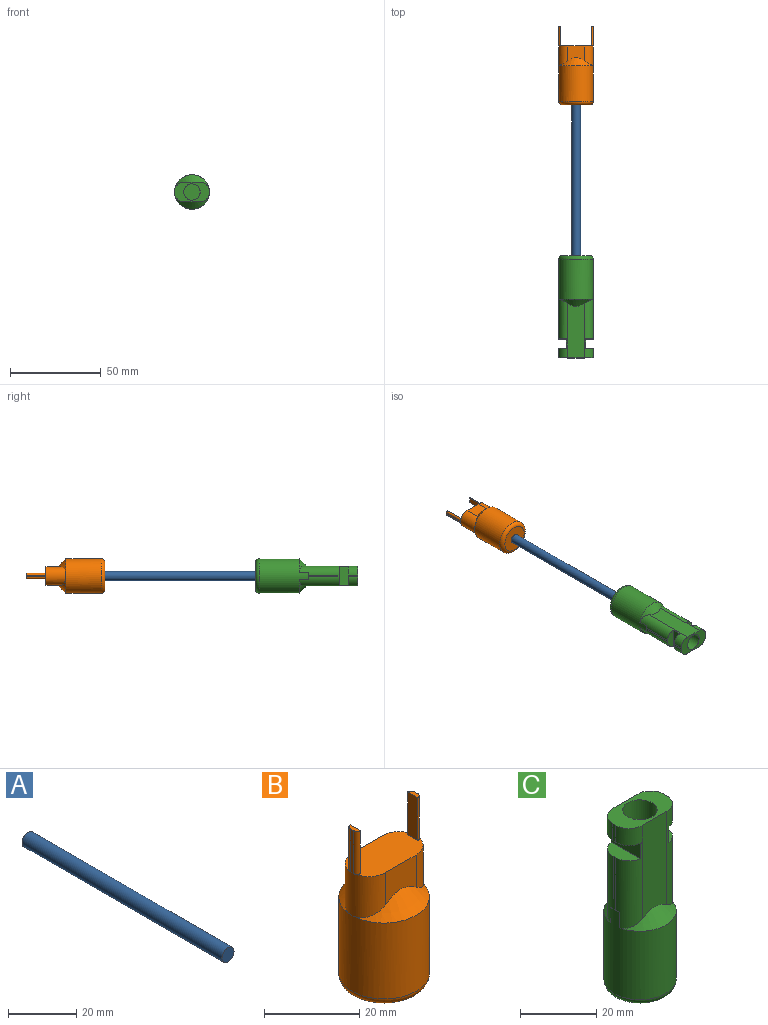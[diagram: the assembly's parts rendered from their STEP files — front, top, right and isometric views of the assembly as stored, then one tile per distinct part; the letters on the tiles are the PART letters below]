
ASSEMBLY  parts=3 mates=2
PART A: 3 faces, bbox 5x83x5 mm
  f0: cylinder r=2.5mm len=83mm, axis (0,1,0), area 1303.8mm2, adj f1,f2
  f1: plane 5x5mm, normal (0,-1,0), area 19.6mm2, adj f0
  f2: plane 5x5mm, normal (0,1,0), area 19.6mm2, adj f0
PART B: 24 faces, bbox 20.6x20.6x43.5 mm
  f0: plane 18.84x10mm, normal (0,0,1), area 163.5mm2, adj f5,f6,f7,f8,f13,f17,f19,f20
  f1: cone r=4.5mm half-angle=45deg, axis (0,0,-1), area 81.3mm2, adj f3,f6,f7,f8
  f2: plane 15x15mm, normal (0,0,-1), area 176.7mm2, adj f23
  f3: cylinder r=9.5mm len=19.5mm, axis (0,0,1), area 1164mm2, adj f1,f4,f23
  f4: cone r=4.5mm half-angle=45deg, axis (0,0,-1), area 81.3mm2, adj f3,f5,f7,f8
  f5: plane 9.01x8.23mm, normal (0,-1,0), area 64mm2, adj f0,f4,f7,f8
  f6: plane 9.01x8.23mm, normal (0,1,0), area 64mm2, adj f0,f1,f7,f8
  f7: cylinder r=5mm len=11mm, axis (0,0,1), area 158mm2, adj f0,f1,f4,f5,f6,f14,f15
  f8: cylinder r=5mm len=11mm, axis (0,0,-1), area 158mm2, adj f0,f1,f4,f5,f6,f9,f10
  f9: plane 0.89x0.08mm, normal (0,0,-1), area 0mm2, adj f8,f11,f20
  f10: plane 0.89x0.08mm, normal (0,0,-1), area 0mm2, adj f8,f11,f19
  f11: plane 11x1mm, normal (1,0,0), area 11mm2, adj f9,f10,f12,f19,f20
  f12: plane 3x1mm, normal (0,0,1), area 2.6mm2, adj f11,f13,f19,f20
  f13: plane 11x3mm, normal (-1,0,0), area 33mm2, adj f0,f12,f19,f20
  f14: plane 0.89x0.08mm, normal (0,0,-1), area 0mm2, adj f7,f16,f21
  f15: plane 0.89x0.08mm, normal (0,0,-1), area 0mm2, adj f7,f16,f22
  f16: plane 11x1mm, normal (-1,0,0), area 11mm2, adj f14,f15,f18,f21,f22
  f17: plane 11x3mm, normal (1,0,0), area 33mm2, adj f0,f18,f21,f22
  f18: plane 3x1mm, normal (0,0,1), area 2.6mm2, adj f16,f17,f21,f22
  f19: cylinder r=1mm len=11mm, axis (0,0,1), area 17.3mm2, adj f0,f10,f11,f12,f13
  f20: cylinder r=1mm len=11mm, axis (0,0,-1), area 17.3mm2, adj f0,f9,f11,f12,f13
  f21: cylinder r=1mm len=11mm, axis (0,0,-1), area 17.3mm2, adj f0,f14,f16,f17,f18
  f22: cylinder r=1mm len=11mm, axis (0,0,1), area 17.3mm2, adj f0,f15,f16,f17,f18
  f23: torus R=7.5mm, axis (0,0,1), area 173.2mm2, adj f2,f3
PART C: 30 faces, bbox 20.6x20.6x56.5 mm
  f0: cylinder r=9.5mm len=27.03mm, axis (0,0,1), area 1351.2mm2, adj f2,f3,f4,f5,f19,f20,f21,f22
  f1: plane 15x15mm, normal (0,0,-1), area 176.7mm2, adj f29
  f2: plane 1.8x0.17mm, normal (0,0,-1), area 0mm2, adj f0,f9,f21
  f3: plane 1.8x0.17mm, normal (0,0,-1), area 0mm2, adj f0,f9,f23
  f4: plane 1.8x0.17mm, normal (0,0,-1), area 0mm2, adj f0,f8,f22
  f5: plane 1.8x0.17mm, normal (0,0,-1), area 0mm2, adj f0,f8,f24
  f6: plane 10.87x5mm, normal (-1,0,0), area 54.4mm2, adj f7,f16,f22,f24
  f7: plane 10.87x4.2mm, normal (0,0,1), area 35.5mm2, adj f6,f8,f22,f24
  f8: plane 16.97x1mm, normal (-1,0,0), area 17mm2, adj f4,f5,f7,f22,f24
  f9: plane 16.97x1mm, normal (1,0,0), area 17mm2, adj f2,f3,f10,f21,f23
  f10: plane 10.87x4.2mm, normal (0,0,1), area 35.5mm2, adj f9,f11,f21,f23
  f11: plane 10.87x5mm, normal (1,0,0), area 54.4mm2, adj f10,f12,f21,f23
  f12: plane 10.87x4.16mm, normal (0,0,-1), area 35.4mm2, adj f11,f13,f21,f23
  f13: plane 5.46x2.29mm, normal (1,0,0), area 12.5mm2, adj f12,f14,f21,f23
  f14: plane 19x11mm, normal (0,0,1), area 124.1mm2, adj f13,f15,f17,f18,f21,f23,f25,f26
  f15: plane 5.46x1mm, normal (-1,0,0), area 5.5mm2, adj f14,f16,f25,f26
  f16: plane 11x5.04mm, normal (0,0,-1), area 36mm2, adj f6,f15,f17,f18,f22,f24,f25,f26
  f17: plane 30.04x9.05mm, normal (0,-1,0), area 261.2mm2, adj f14,f16,f20,f23,f24,f26
  f18: plane 30.04x9.05mm, normal (0,1,0), area 261.2mm2, adj f14,f16,f19,f21,f22,f25
  f19: cone r=9.5mm half-angle=45deg, axis (0,0,-1), area 68mm2, adj f0,f18,f21,f22
  f20: cone r=9.5mm half-angle=45deg, axis (0,0,-1), area 68mm2, adj f0,f17,f23,f24
  f21: cylinder r=5mm len=32.43mm, axis (0,0,1), area 203.5mm2, adj f0,f2,f9,f10,f11,f12,f13,f14
  f22: cylinder r=5mm len=26.97mm, axis (0,0,-1), area 164.2mm2, adj f0,f4,f6,f7,f8,f16,f18,f19
  f23: cylinder r=5mm len=32.43mm, axis (0,0,-1), area 203.5mm2, adj f0,f3,f9,f10,f11,f12,f13,f14
  f24: cylinder r=5mm len=26.97mm, axis (0,0,1), area 164.2mm2, adj f0,f5,f6,f7,f8,f16,f17,f20
  f25: cylinder r=5mm len=5.46mm, axis (0,0,-1), area 42.9mm2, adj f14,f15,f16,f18
  f26: cylinder r=5mm len=5.46mm, axis (0,0,1), area 42.9mm2, adj f14,f15,f16,f17
  f27: cylinder r=4.51mm len=10mm, axis (0,0,1), area 283.3mm2, adj f14,f28
  f28: plane 9.02x9.02mm, normal (0,0,1), area 63.9mm2, adj f27
  f29: torus R=7.5mm, axis (0,0,1), area 173.2mm2, adj f0,f1
PLACE A t=(-389.08,66.26,-41.09)mm
PLACE B rot(axis=(-1,0,0),90deg) t=(-352.89,224.95,-9.02)mm
PLACE C rot(axis=(1,0,0),90deg) t=(-432.11,-151.43,-9.02)mm
MATE fastened C.f0 <-> A.f0  axis (0,1,0) through (16.93,-16.74,-9.02)mm
MATE fastened B.f1 <-> A.f0  axis (0,-1,0) through (16.93,66.26,-9.02)mm
